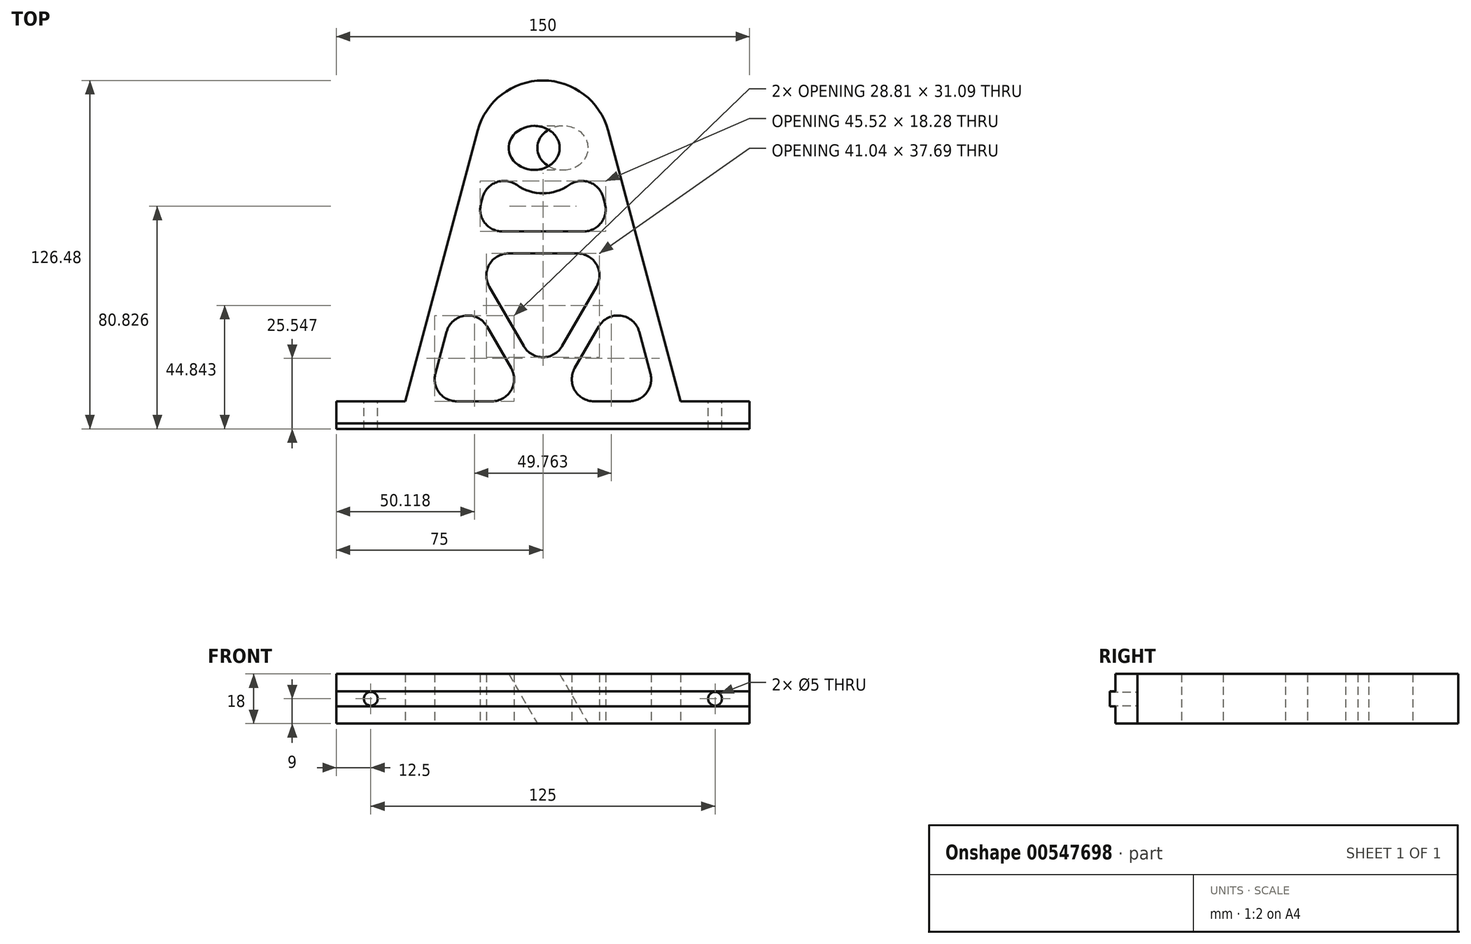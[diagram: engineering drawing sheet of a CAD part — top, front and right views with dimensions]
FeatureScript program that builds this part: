
annotation { "Feature Type Name" : "Feature", "Feature Type Description" : "" }
export const myFeature = defineFeature(function(context is Context, id is Id, definition is map)
    precondition{}
    {
        {
            var Q0;
            Q0=qCreatedBy(makeId("Top.planeOp"),FACE);
            var sketch = newSketch(context, id + "F0", { "sketchPlane" : qUnion([Q0])});
            skLineSegment(sketch, "E0.bottom", {"start": v(75, -4) * mm, "end": v(-75, -4) * mm});
            skLineSegment(sketch, "E0.top", {"start": v(31.3, 4) * mm, "end": v(18.48, 4) * mm});
            skLineSegment(sketch, "E0.left", {"start": v(75, -4) * mm, "end": v(75, 4) * mm});
            skLineSegment(sketch, "E0.right", {"start": v(-75, -4) * mm, "end": v(-75, 4) * mm});
            skPoint(sketch, "E0.middle", {"position": v(0, 0) * mm});
            skLineSegment(sketch, "E1", {"start": v(-50, 4) * mm, "end": v(-23.65, 102.34) * mm});
            skLineSegment(sketch, "E2", {"start": v(23.65, 102.34) * mm, "end": v(50, 4) * mm});
            skLineSegment(sketch, "E3", {"start": v(-39.02, 14.07) * mm, "end": v(-34.96, 29.23) * mm});
            skLineSegment(sketch, "E4", {"start": v(34.96, 29.23) * mm, "end": v(39.02, 14.07) * mm});
            skLineSegment(sketch, "E5", {"start": v(20.3, 31.16) * mm, "end": v(11.55, 16) * mm});
            skLineSegment(sketch, "E6", {"start": v(-11.55, 16) * mm, "end": v(-20.3, 31.16) * mm});
            skLineSegment(sketch, "E7", {"start": v(-25.38, 39.95) * mm, "end": v(-29.96, 47.89) * mm});
            skLineSegment(sketch, "E8", {"start": v(-12.52, 57.69) * mm, "end": v(12.52, 57.69) * mm});
            skLineSegment(sketch, "E9", {"start": v(-14.76, 65.69) * mm, "end": v(14.76, 65.69) * mm});
            skLineSegment(sketch, "E10", {"start": v(-6.93, 24) * mm, "end": v(-19.45, 45.69) * mm});
            skLineSegment(sketch, "E11", {"start": v(6.93, 24) * mm, "end": v(19.45, 45.69) * mm});
            skPoint(sketch, "E12.newPointB", {"position": v(-75, 4) * mm});
            skArc(sketch, "E12.filletArc", {"start": v(-39.02, 14.07) * mm, "mid": v(-37.64, 7.13) * mm, "end": v(-31.3, 4) * mm});
            skPoint(sketch, "E13.newPointA", {"position": v(75, 4) * mm});
            skArc(sketch, "E13.filletArc", {"start": v(31.3, 4) * mm, "mid": v(37.64, 7.13) * mm, "end": v(39.02, 14.07) * mm});
            skArc(sketch, "E14.filletArc", {"start": v(34.96, 29.23) * mm, "mid": v(28.27, 35.1) * mm, "end": v(20.3, 31.16) * mm});
            skPoint(sketch, "E15.newPointA", {"position": v(0, -4) * mm});
            skArc(sketch, "E15.filletArc", {"start": v(11.55, 16) * mm, "mid": v(11.55, 8) * mm, "end": v(18.48, 4) * mm});
            skArc(sketch, "E16.filletArc", {"start": v(19.45, 45.69) * mm, "mid": v(19.45, 53.69) * mm, "end": v(12.52, 57.69) * mm});
            skArc(sketch, "E17.filletArc", {"start": v(-12.52, 57.69) * mm, "mid": v(-19.45, 53.69) * mm, "end": v(-19.45, 45.69) * mm});
            skArc(sketch, "E18.filletArc", {"start": v(-6.93, 24) * mm, "mid": v(0, 20) * mm, "end": v(6.93, 24) * mm});
            skLineSegment(sketch, "E19", {"start": v(-31.3, 4) * mm, "end": v(-18.48, 4) * mm});
            skArc(sketch, "E20.filletArc", {"start": v(-18.48, 4) * mm, "mid": v(-11.55, 8) * mm, "end": v(-11.55, 16) * mm});
            skLineSegment(sketch, "E21", {"start": v(-75, 4) * mm, "end": v(-50, 4) * mm});
            skLineSegment(sketch, "E22", {"start": v(50, 4) * mm, "end": v(75, 4) * mm});
            skLineSegment(sketch, "E23.trimOffspring", {"start": v(-22.5, 75.76) * mm, "end": v(-21.87, 78.08) * mm});
            skLineSegment(sketch, "E24", {"start": v(21.87, 78.08) * mm, "end": v(22.5, 75.76) * mm});
            skArc(sketch, "E25", {"start": v(-9.52, 82.54) * mm, "mid": v(0, 79.52) * mm, "end": v(9.52, 82.54) * mm});
            skArc(sketch, "E26", {"start": v(23.65, 102.34) * mm, "mid": v(0, 120.48) * mm, "end": v(-23.65, 102.34) * mm});
            skPoint(sketch, "E27.orphan", {"position": v(0, 190.6) * mm});
            skPoint(sketch, "E28.orphan", {"position": v(0, 159.7) * mm});
            skPoint(sketch, "E29.end.orphan", {"position": v(0, 65.69) * mm});
            skArc(sketch, "E30.filletArc", {"start": v(-22.5, 75.76) * mm, "mid": v(-21.1, 68.82) * mm, "end": v(-14.76, 65.69) * mm});
            skArc(sketch, "E31.filletArc", {"start": v(14.76, 65.69) * mm, "mid": v(21.1, 68.82) * mm, "end": v(22.5, 75.76) * mm});
            skArc(sketch, "E32", {"start": v(-9.52, 82.54) * mm, "mid": v(-16.86, 83.54) * mm, "end": v(-21.87, 78.08) * mm});
            skArc(sketch, "E33", {"start": v(21.87, 78.08) * mm, "mid": v(16.86, 83.54) * mm, "end": v(9.52, 82.54) * mm});
            skPoint(sketch, "E34.visualSharp", {"position": v(-29.96, 47.89) * mm});
            skArc(sketch, "E34.filletArc", {"start": v(-20.3, 31.16) * mm, "mid": v(-28.27, 35.1) * mm, "end": v(-34.96, 29.23) * mm});
            skSolve(sketch);
        }
        {
            var Q0;
            Q0=qCreatedBy(makeId("Front.planeOp"),FACE);
            cPlane(context, id + "F1", {"entities" : qUnion([Q0]), "cplaneType" : CPlaneType.OFFSET, "offset" : 96 * mm, "oppositeDirection" : true, "width" : 150 * mm, "height" : 150 * mm});
        }
        {
            var Q0;
            Q0=qCreatedBy(id+"F1.planeOp",FACE);
            var sketch = newSketch(context, id + "F2", { "sketchPlane" : qUnion([Q0])});
            skLineSegment(sketch, "E35", {"start": v(0, 0) * mm, "end": v(12.59, 0) * mm});
            skLineSegment(sketch, "E36", {"start": v(12.59, 0) * mm, "end": v(12.59, -21.8) * mm});
            skLineSegment(sketch, "E37", {"start": v(12.59, -21.8) * mm, "end": v(0, 0) * mm});
            skLineSegment(sketch, "E38", {"start": v(12.59, 0) * mm, "end": v(3.15, -5.45) * mm});
            skSolve(sketch);
        }
        {
            var Q0;
            Q0=sQuery(id+"F2.wireOp",EDGE,"E37");
            cPlane(context, id + "F3", {"entities" : qUnion([Q0]), "cplaneType" : CPlaneType.LINE_ANGLE, "offset" : 25 * mm, "angle" : 0 * degree, "width" : 150 * mm, "height" : 150 * mm});
        }
        {
            var Q0;
            Q0=sQuery(id+"F2.wireOp",EDGE,"E38");
            var Q1;
            Q1=qCreatedBy(id+"F1.planeOp",FACE);
            cPlane(context, id + "F4", {"entities" : qUnion([Q0, Q1]), "cplaneType" : CPlaneType.LINE_ANGLE, "offset" : 25 * mm, "angle" : 90 * degree, "width" : 150 * mm, "height" : 150 * mm});
        }
        {
            var Q0;
            Q0=qCreatedBy(id+"F4.planeOp",FACE);
            var sketch = newSketch(context, id + "F5", { "sketchPlane" : qUnion([Q0])});
            skPoint(sketch, "E39.center.orphan", {"position": v(0, -295.6) * mm});
            skCircle(sketch, "E40", {"center": v(6.25, -96) * mm, "radius": 8 * mm});
            skSolve(sketch);
        }
        {
            var Q0;
            Q0=makeQuery(id+"F0.imprint","IMPRINT",FACE,{"disambiguationData":[TD([[makeQuery(id+"F0.imprint","IMPRINT",EDGE,{"derivedFrom":sQuery(id+"F0.wireOp",EDGE,"E0.bottom")}),-1.0]])]});
            extrude(context, id + "F6", {"entities" : qUnion([Q0]), "depth" : 18 * mm, "offsetDistance" : 25 * mm});
        }
        {
            var Q0;
            Q0=makeQuery(id+"F6.opExtrude","SWEPT_FACE",FACE,{"disambiguationData":[OSD([sQuery(id+"F0.wireOp",EDGE,"E0.bottom")])]});
            var sketch = newSketch(context, id + "F7", { "sketchPlane" : qUnion([Q0])});
            skLineSegment(sketch, "E41.bottom", {"start": v(75, 6.25) * mm, "end": v(-75, 6.25) * mm});
            skLineSegment(sketch, "E41.top", {"start": v(75, 11.75) * mm, "end": v(-75, 11.75) * mm});
            skLineSegment(sketch, "E41.left", {"start": v(75, 6.25) * mm, "end": v(75, 11.75) * mm});
            skLineSegment(sketch, "E41.right", {"start": v(-75, 6.25) * mm, "end": v(-75, 11.75) * mm});
            skCircle(sketch, "E42", {"center": v(62.5, 9) * mm, "radius": 2.5 * mm});
            skCircle(sketch, "E43", {"center": v(-62.5, 9) * mm, "radius": 2.5 * mm});
            skSolve(sketch);
        }
        {
            var Q0;
            Q0=makeQuery(id+"F7.imprint","IMPRINT",FACE,{"disambiguationData":[TD([[makeQuery(id+"F7.imprint","IMPRINT",EDGE,{"derivedFrom":sQuery(id+"F7.wireOp",EDGE,"E41.bottom")}),-1.0]])]});
            extrude(context, id + "F8", {"entities" : qUnion([Q0]), "operationType" : NewBodyOperationType.ADD, "depth" : 2 * mm, "offsetDistance" : 25 * mm});
        }
        {
            var Q0;
            Q0=makeQuery(id+"F8.boolean.opBoolean","SPLIT",FACE,{"disambiguationData":[TD([makeQuery(id+"F8.opExtrude","SWEPT_FACE",FACE,{"disambiguationData":[OSD([sQuery(id+"F7.wireOp",EDGE,"E42")])]})])],"derivedFrom":makeQuery(id+"F6.opExtrude","SWEPT_FACE",FACE,{"disambiguationData":[OSD([sQuery(id+"F0.wireOp",EDGE,"E0.bottom")])]})});
            var Q1;
            Q1=makeQuery(id+"F8.boolean.opBoolean","SPLIT",FACE,{"disambiguationData":[TD([makeQuery(id+"F8.opExtrude","SWEPT_FACE",FACE,{"disambiguationData":[OSD([sQuery(id+"F7.wireOp",EDGE,"E43")])]})])],"derivedFrom":makeQuery(id+"F6.opExtrude","SWEPT_FACE",FACE,{"disambiguationData":[OSD([sQuery(id+"F0.wireOp",EDGE,"E0.bottom")])]})});
            extrude(context, id + "F9", {"entities" : qUnion([Q0, Q1]), "operationType" : NewBodyOperationType.REMOVE, "oppositeDirection" : true, "depth" : 8 * mm, "offsetDistance" : 25 * mm});
        }
        {
            var Q0;
            Q0=makeQuery(id+"F5.imprint","IMPRINT",FACE,{"disambiguationData":[TD([[makeQuery(id+"F5.imprint","IMPRINT",EDGE,{"derivedFrom":sQuery(id+"F5.wireOp",EDGE,"E40")}),1.0]])]});
            extrude(context, id + "F10", {"entities" : qUnion([Q0]), "operationType" : NewBodyOperationType.REMOVE, "oppositeDirection" : true, "depth" : 40 * mm, "offsetDistance" : 25 * mm, "hasSecondDirection" : true, "secondDirectionOppositeDirection" : false, "secondDirectionDepth" : 30 * mm});
        }
    });
